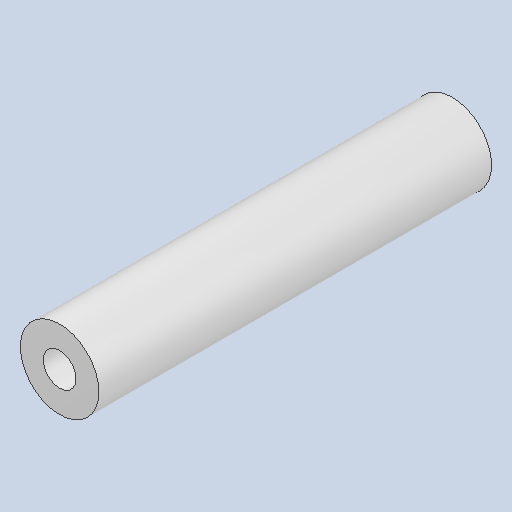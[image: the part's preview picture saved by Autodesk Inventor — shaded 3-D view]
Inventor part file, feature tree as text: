
AUTODESK INVENTOR PART (.ipt)
format: ipt  version: 2023 (Build 270158030, 158C)  size: 227,840 bytes
history: native  units: mm
features: extrude x1, sketch x1
ambient origin geometry x8: Origin, YZ Plane, XZ Plane, XY Plane, X Axis, Y Axis, Z Axis, Center Point
bodies: Solid1 (feature_tree)
feature tree (2):
  extrude  "Extrusion1"  Depth=30.0mm
  sketch  "Sketch1"  dims[d0=2.5mm d1=6.0mm d2=30.0mm d3=0.0mm]
